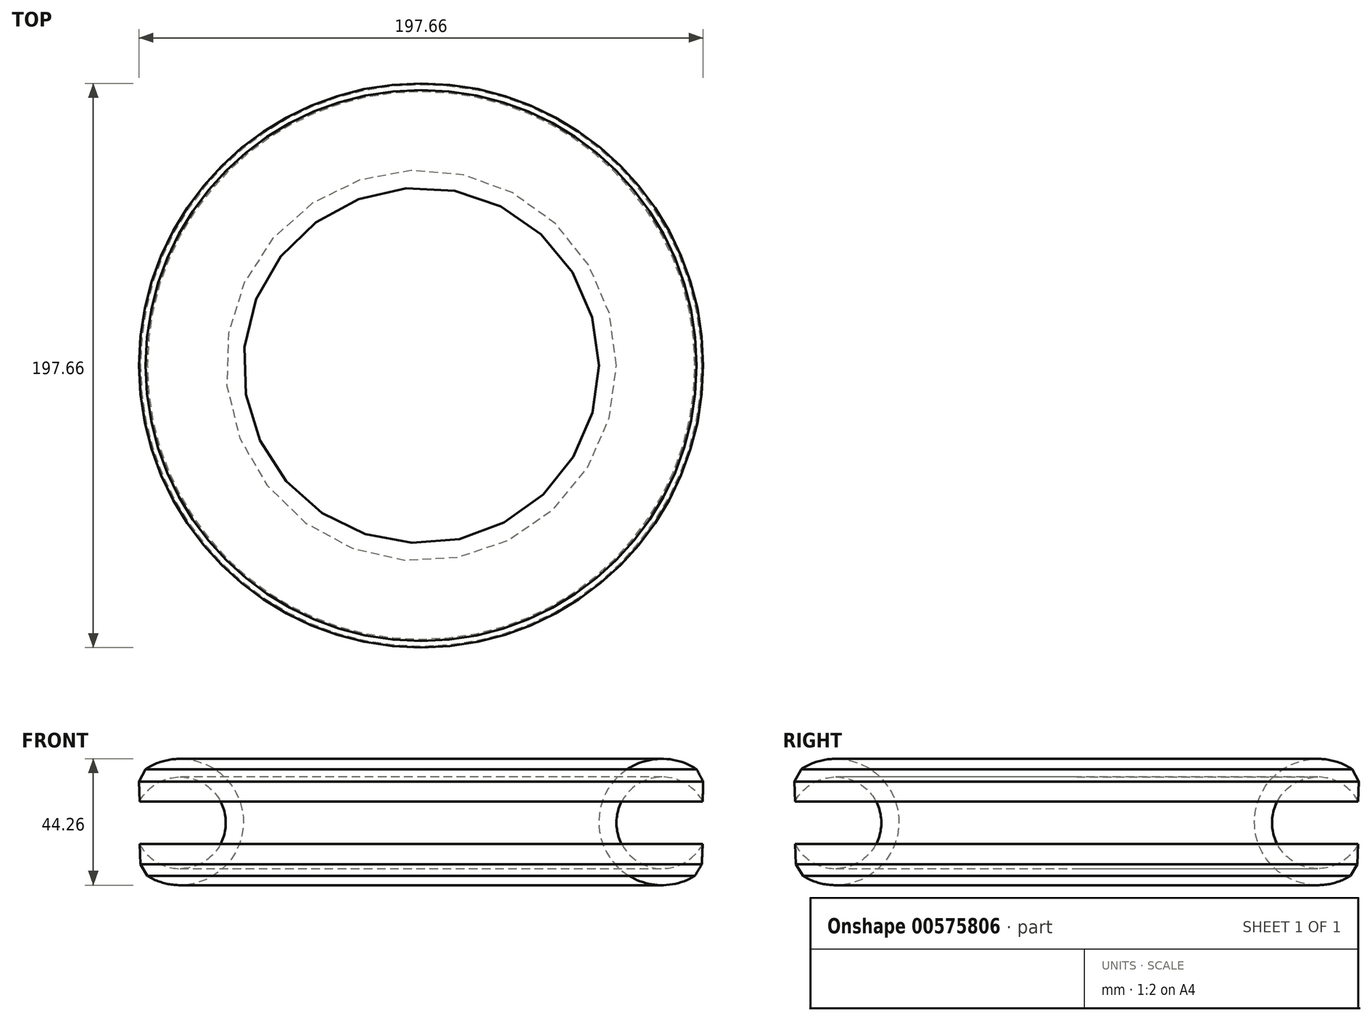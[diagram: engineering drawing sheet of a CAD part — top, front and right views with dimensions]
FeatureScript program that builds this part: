
annotation { "Feature Type Name" : "Feature", "Feature Type Description" : "" }
export const myFeature = defineFeature(function(context is Context, id is Id, definition is map)
    precondition{}
    {
        {
            var Q0;
            Q0=qCreatedBy(makeId("Right.planeOp"),FACE);
            var sketch = newSketch(context, id + "F0", { "sketchPlane" : qUnion([Q0])});
            skLineSegment(sketch, "E0", {"start": v(0, 18.9) * mm, "end": v(0, -17.58) * mm});
            skLineSegment(sketch, "E1", {"start": v(98.9, 16.72) * mm, "end": v(98.64, 7.2) * mm});
            skLineSegment(sketch, "E2", {"start": v(98.64, -7.76) * mm, "end": v(98.22, -17.29) * mm});
            skArc(sketch, "E3", {"start": v(98.64, 7.2) * mm, "mid": v(68.43, -0.28) * mm, "end": v(98.64, -7.76) * mm});
            skArc(sketch, "E4", {"start": v(98.9, 16.72) * mm, "mid": v(62.27, 0.44) * mm, "end": v(98.22, -17.29) * mm});
            skSolve(sketch);
        }
        {
            var Q0;
            Q0=makeQuery(id+"F0.imprint","IMPRINT",FACE,{"disambiguationData":[TD([[makeQuery(id+"F0.imprint","IMPRINT",EDGE,{"derivedFrom":sQuery(id+"F0.wireOp",EDGE,"E1")}),-1.0]])]});
            var Q1;
            Q1=sQuery(id+"F0.wireOp",EDGE,"E0");
            revolve(context, id + "F1", {"entities" : qUnion([Q0]), "axis" : qUnion([Q1]), "revolveType" : RevolveType.FULL});
        }
        {
            var Q0;
            Q0=makeQuery(id+"F1.opRevolve","SWEPT_FACE",FACE,{"disambiguationData":[OSD([sQuery(id+"F0.wireOp",EDGE,"E4")])]});
            chamfer(context, id + "F2", {"entities" : qUnion([Q0]), "width" : 5.08 * mm, "tangentPropagation" : true});
        }
    });
